FCSTD DOCUMENT  (FreeCAD 0.22R34729 (Git))
Label: PC817_C231F
License: All rights reserved
LicenseURL: http://en.wikipedia.org/wiki/All_rights_reserved
objects: Sketcher::SketchObject×2
note: 2 computed .brp shape members not serialized (recipe doc carries the construction recipe); baked Part::Feature solids carry a one-line shape summary decoded from their .brp

FEATURE [Sketcher::SketchObject] Sketch  label="legs_sketch"
  FullyConstrained = true
  sketch-geometry (9):
    g0: LineSegment StartX=-1.27 StartY=-3.81 StartZ=0 EndX=-1.27 EndY=3.81 EndZ=0
    g1: LineSegment StartX=-1.27 StartY=3.81 StartZ=0 EndX=1.27 EndY=3.81 EndZ=0
    g2: LineSegment StartX=1.27 StartY=3.81 StartZ=0 EndX=1.27 EndY=-3.81 EndZ=0
    g3: LineSegment StartX=1.27 StartY=-3.81 StartZ=0 EndX=-1.27 EndY=-3.81 EndZ=0
    g4: GeomPoint X=0 Y=0 Z=0
    g5: Circle CenterX=1.27 CenterY=3.81 CenterZ=0 NormalX=0 NormalY=0 NormalZ=1 AngleXU=0 Radius=0.2
    g6: Circle CenterX=-1.27 CenterY=3.81 CenterZ=0 NormalX=0 NormalY=0 NormalZ=1 AngleXU=0 Radius=0.2
    g7: Circle CenterX=-1.27 CenterY=-3.81 CenterZ=0 NormalX=0 NormalY=0 NormalZ=1 AngleXU=0 Radius=0.2
    g8: Circle CenterX=1.27 CenterY=-3.81 CenterZ=0 NormalX=0 NormalY=0 NormalZ=1 AngleXU=0 Radius=0.2
  constraints (20):
    c: Coincident(g0,g1)
    c: Coincident(g1,g2)
    c: Coincident(g2,g3)
    c: Coincident(g3,g0)
    c: Horizontal(g1)
    c: Horizontal(g3)
    c: Vertical(g0)
    c: Vertical(g2)
    c: Symmetric(g1,g0,g4)
    c: Coincident(g4,g-1)
    c: Coincident(g5,g1)
    c: Coincident(g6,g0)
    c: Coincident(g7,g0)
    c: Coincident(g8,g2)
    c: DistanceX(g1,g1) = 2.54
    c: DistanceY(g2,g2) = 7.62
    c: Equal(g5,g6)
    c: Equal(g5,g7)
    c: Equal(g5,g8)
    c: Diameter(g5) = 0.4
FEATURE [Sketcher::SketchObject] Sketch001  label="base_sketch"
  FullyConstrained = true
  sketch-geometry (5):
    g0: LineSegment StartX=-2.29 StartY=-3.25 StartZ=0 EndX=-2.29 EndY=3.25 EndZ=0
    g1: LineSegment StartX=-2.29 StartY=3.25 StartZ=0 EndX=2.29 EndY=3.25 EndZ=0
    g2: LineSegment StartX=2.29 StartY=3.25 StartZ=0 EndX=2.29 EndY=-3.25 EndZ=0
    g3: LineSegment StartX=2.29 StartY=-3.25 StartZ=0 EndX=-2.29 EndY=-3.25 EndZ=0
    g4: GeomPoint X=0 Y=0 Z=0
  constraints (12):
    c: Coincident(g0,g1)
    c: Coincident(g1,g2)
    c: Coincident(g2,g3)
    c: Coincident(g3,g0)
    c: Horizontal(g1)
    c: Horizontal(g3)
    c: Vertical(g0)
    c: Vertical(g2)
    c: Symmetric(g1,g0,g4)
    c: Coincident(g4,g-1)
    c: DistanceY(g2,g2) = 6.5  'width'
    c: DistanceX(g1,g1) = 4.58  'length'
